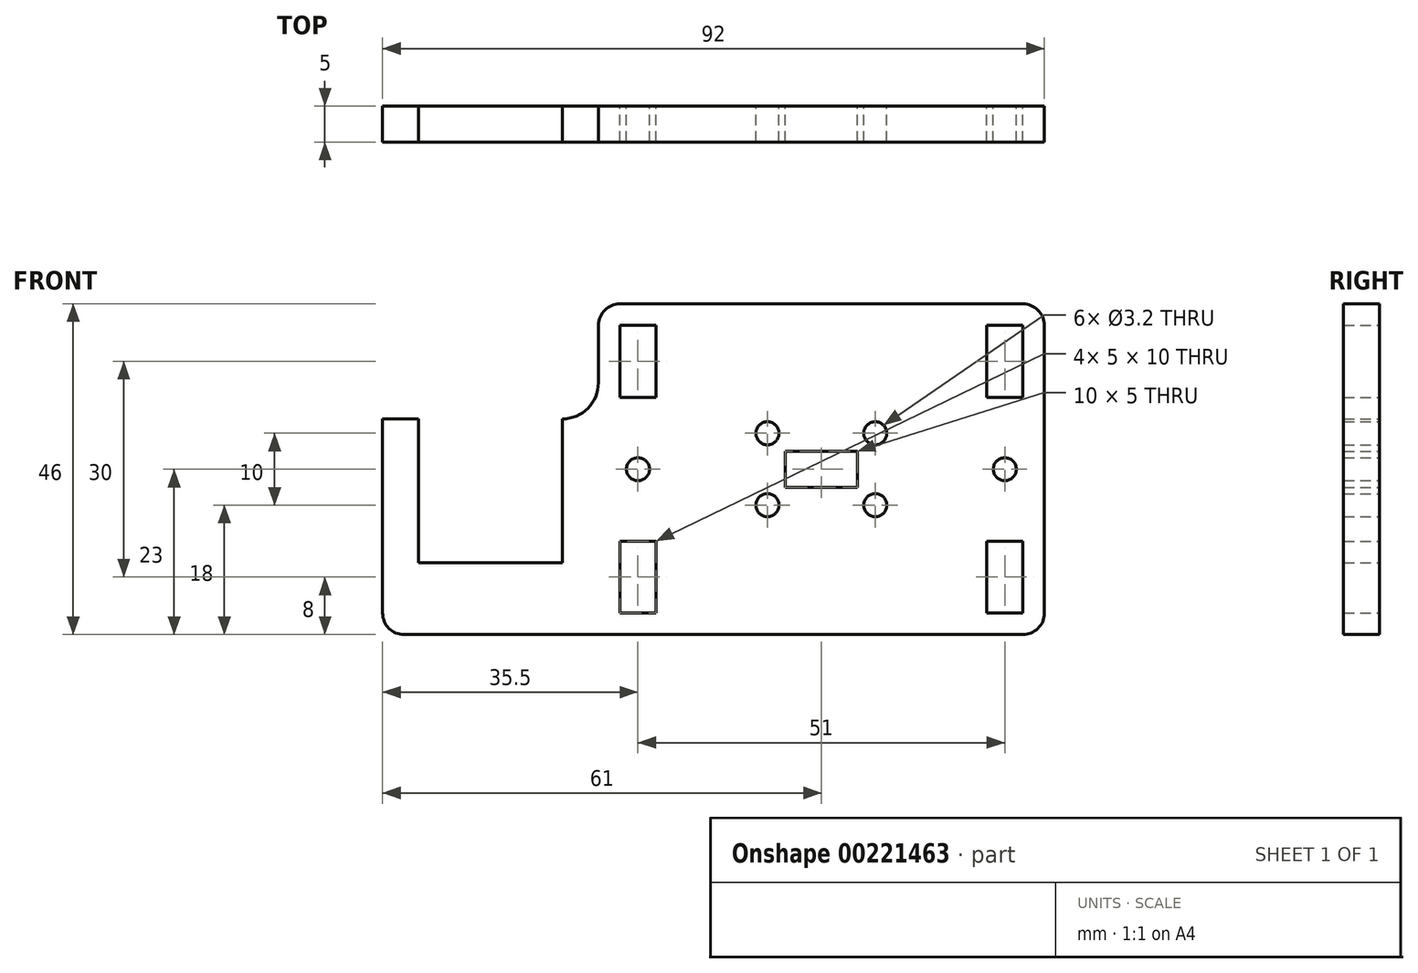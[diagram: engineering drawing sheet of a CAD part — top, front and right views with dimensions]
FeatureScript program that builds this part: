
annotation { "Feature Type Name" : "Feature", "Feature Type Description" : "" }
export const myFeature = defineFeature(function(context is Context, id is Id, definition is map)
    precondition{}
    {
        {
            assignVariable(context, id + "F0", {"name" : "thickness", "anyValue" : 5 * mm});
        }
        {
            var Q0;
            Q0=qCreatedBy(makeId("Front.planeOp"),FACE);
            var sketch = newSketch(context, id + "F1", { "sketchPlane" : qUnion([Q0])});
            skLineSegment(sketch, "E0.bottom", {"start": v(0, 0) * mm, "end": v(20, 0) * mm, "construction": true});
            skLineSegment(sketch, "E0.top", {"start": v(0, 30) * mm, "end": v(20, 30) * mm, "construction": true});
            skLineSegment(sketch, "E0.left", {"start": v(0, 0) * mm, "end": v(0, 30) * mm, "construction": true});
            skLineSegment(sketch, "E0.right", {"start": v(20, 0) * mm, "end": v(20, 30) * mm, "construction": true});
            skLineSegment(sketch, "E1.bottom", {"start": v(2.5, 20) * mm, "end": v(17.5, 20) * mm, "construction": true});
            skLineSegment(sketch, "E1.top", {"start": v(2.5, 10) * mm, "end": v(17.5, 10) * mm, "construction": true});
            skLineSegment(sketch, "E1.left", {"start": v(2.5, 20) * mm, "end": v(2.5, 10) * mm, "construction": true});
            skLineSegment(sketch, "E1.right", {"start": v(17.5, 20) * mm, "end": v(17.5, 10) * mm, "construction": true});
            skPoint(sketch, "E2", {"position": v(10, 30) * mm});
            skPoint(sketch, "E3", {"position": v(10, 20) * mm});
            skPoint(sketch, "E4", {"position": v(2.5, 15) * mm});
            skPoint(sketch, "E5", {"position": v(0, 15) * mm});
            skCircle(sketch, "E6", {"center": v(2.5, 20) * mm, "radius": 1.6 * mm});
            skCircle(sketch, "E7", {"center": v(17.5, 20) * mm, "radius": 1.6 * mm});
            skCircle(sketch, "E8", {"center": v(17.5, 10) * mm, "radius": 1.6 * mm});
            skCircle(sketch, "E9", {"center": v(2.5, 10) * mm, "radius": 1.6 * mm});
            skLineSegment(sketch, "E10.0", {"start": v(-21, 27) * mm, "end": v(-21, 35) * mm});
            skLineSegment(sketch, "E10.2", {"start": v(41, -5) * mm, "end": v(41, 35) * mm});
            skLineSegment(sketch, "E11.bottom", {"start": v(-18, 35) * mm, "end": v(-13, 35) * mm});
            skLineSegment(sketch, "E11.top", {"start": v(-18, 25) * mm, "end": v(-13, 25) * mm});
            skLineSegment(sketch, "E11.left", {"start": v(-18, 35) * mm, "end": v(-18, 25) * mm});
            skLineSegment(sketch, "E11.right", {"start": v(-13, 35) * mm, "end": v(-13, 25) * mm});
            skLineSegment(sketch, "E12", {"start": v(-21, 15) * mm, "end": v(41, 15) * mm, "construction": true});
            skLineSegment(sketch, "E13.MirrorCS", {"start": v(-18, -5) * mm, "end": v(-18, 5) * mm});
            skLineSegment(sketch, "E14.MirrorCS", {"start": v(-18, -5) * mm, "end": v(-13, -5) * mm});
            skLineSegment(sketch, "E15.MirrorCS", {"start": v(-13, -5) * mm, "end": v(-13, 5) * mm});
            skLineSegment(sketch, "E16.MirrorCS", {"start": v(-18, 5) * mm, "end": v(-13, 5) * mm});
            skLineSegment(sketch, "E17", {"start": v(10, 38) * mm, "end": v(10, -8) * mm, "construction": true});
            skLineSegment(sketch, "E18.MirrorCS", {"start": v(38, 35) * mm, "end": v(33, 35) * mm});
            skLineSegment(sketch, "E19.MirrorCS", {"start": v(38, 35) * mm, "end": v(38, 25) * mm});
            skLineSegment(sketch, "E20.MirrorCS", {"start": v(33, 35) * mm, "end": v(33, 25) * mm});
            skLineSegment(sketch, "E21.MirrorCS", {"start": v(38, 25) * mm, "end": v(33, 25) * mm});
            skLineSegment(sketch, "E22.MirrorCS", {"start": v(38, -5) * mm, "end": v(38, 5) * mm});
            skLineSegment(sketch, "E23.MirrorCS", {"start": v(38, 5) * mm, "end": v(33, 5) * mm});
            skLineSegment(sketch, "E24.MirrorCS", {"start": v(33, -5) * mm, "end": v(33, 5) * mm});
            skLineSegment(sketch, "E25.MirrorCS", {"start": v(38, -5) * mm, "end": v(33, -5) * mm});
            skCircle(sketch, "E26", {"center": v(-15.5, 15) * mm, "radius": 1.6 * mm});
            skPoint(sketch, "E27", {"position": v(-15.5, 25) * mm});
            skCircle(sketch, "E28.MirrorC", {"center": v(35.5, 15) * mm, "radius": 1.6 * mm});
            skLineSegment(sketch, "E29.bottom", {"start": v(5, 17.5) * mm, "end": v(15, 17.5) * mm});
            skLineSegment(sketch, "E29.top", {"start": v(5, 12.5) * mm, "end": v(15, 12.5) * mm});
            skLineSegment(sketch, "E29.left", {"start": v(5, 17.5) * mm, "end": v(5, 12.5) * mm});
            skLineSegment(sketch, "E29.right", {"start": v(15, 17.5) * mm, "end": v(15, 12.5) * mm});
            skPoint(sketch, "E30", {"position": v(5, 15) * mm});
            skPoint(sketch, "E31", {"position": v(10, 17.5) * mm});
            skLineSegment(sketch, "E32", {"start": v(-18, 38) * mm, "end": v(38, 38) * mm});
            skLineSegment(sketch, "E33", {"start": v(-48, -8) * mm, "end": v(38, -8) * mm});
            skPoint(sketch, "E34.visualSharp", {"position": v(-21, 38) * mm});
            skArc(sketch, "E34.filletArc", {"start": v(-18, 38) * mm, "mid": v(-20.12, 37.12) * mm, "end": v(-21, 35) * mm});
            skPoint(sketch, "E35.visualSharp", {"position": v(41, 38) * mm});
            skArc(sketch, "E35.filletArc", {"start": v(41, 35) * mm, "mid": v(40.12, 37.12) * mm, "end": v(38, 38) * mm});
            skPoint(sketch, "E36.visualSharp", {"position": v(-21, -8) * mm});
            skPoint(sketch, "E37.visualSharp", {"position": v(41, -8) * mm});
            skArc(sketch, "E37.filletArc", {"start": v(38, -8) * mm, "mid": v(40.12, -7.12) * mm, "end": v(41, -5) * mm});
            skLineSegment(sketch, "E38", {"start": v(-51, 22) * mm, "end": v(-51, -5) * mm});
            skLineSegment(sketch, "E39.0", {"start": v(-46, 2) * mm, "end": v(-26, 2) * mm});
            skLineSegment(sketch, "E40", {"start": v(-26, 22) * mm, "end": v(-26, 2) * mm});
            skPoint(sketch, "E41.visualSharp", {"position": v(-51, -8) * mm});
            skArc(sketch, "E41.filletArc", {"start": v(-51, -5) * mm, "mid": v(-50.12, -7.12) * mm, "end": v(-48, -8) * mm});
            skPoint(sketch, "E42.visualSharp", {"position": v(-21, 22) * mm});
            skArc(sketch, "E42.filletArc", {"start": v(-26, 22) * mm, "mid": v(-22.46, 23.46) * mm, "end": v(-21, 27) * mm});
            skLineSegment(sketch, "E43", {"start": v(-46, 2) * mm, "end": v(-46, 22) * mm});
            skLineSegment(sketch, "E44", {"start": v(-46, 22) * mm, "end": v(-51, 22) * mm});
            skSolve(sketch);
        }
        {
            var Q0;
            Q0 = qSketchRegion(id + "F1", true);
            extrude(context, id + "F2", {"entities" : qUnion([Q0]), "depth" : getVariable(context, 'thickness')});
        }
    });
